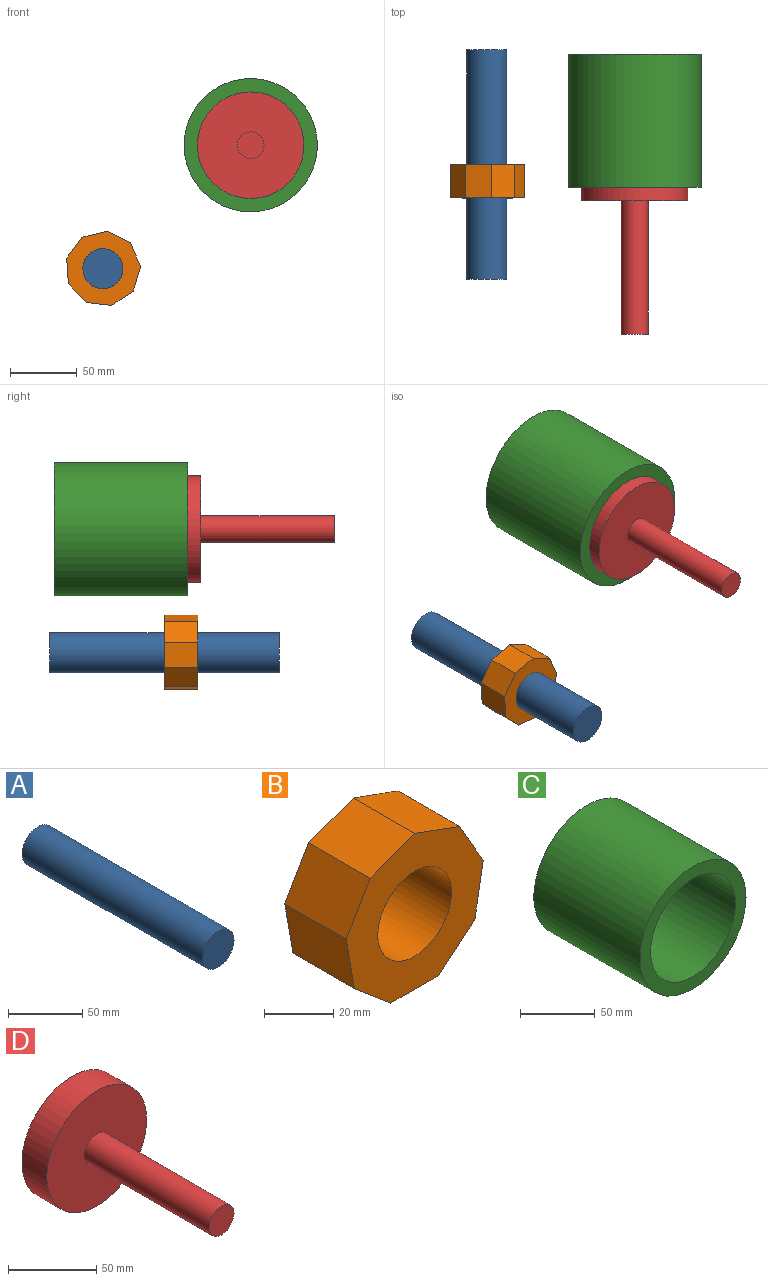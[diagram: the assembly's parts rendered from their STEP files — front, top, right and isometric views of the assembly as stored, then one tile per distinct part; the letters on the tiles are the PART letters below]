
ASSEMBLY  parts=4 mates=2
PART A: 3 faces, bbox 30x172.1x30 mm
  f0: cylinder r=15mm len=172.1mm, axis (0,1,0), area 16220mm2, adj f1,f2
  f1: plane 30x30mm, normal (0,-1,0), area 706.9mm2, adj f0
  f2: plane 30x30mm, normal (0,1,0), area 706.9mm2, adj f0
PART B: 12 faces, bbox 55.8x25x55 mm
  f0: plane 25x14.85mm, normal (0.64,0,-0.77), area 484.6mm2, adj f1,f8,f9,f10
  f1: plane 25x19.09mm, normal (0.98,0,-0.17), area 484.6mm2, adj f0,f2,f9,f10
  f2: plane 25x16.79mm, normal (0.87,0,0.5), area 484.6mm2, adj f1,f3,f9,f10
  f3: plane 25x18.21mm, normal (0.34,0,0.94), area 484.6mm2, adj f2,f4,f9,f10
  f4: plane 25x18.21mm, normal (-0.34,0,0.94), area 484.6mm2, adj f3,f5,f9,f10
  f5: plane 25x16.79mm, normal (-0.87,0,0.5), area 484.6mm2, adj f4,f6,f9,f10
  f6: plane 25x19.09mm, normal (-0.98,0,-0.17), area 484.6mm2, adj f5,f7,f9,f10
  f7: plane 25x14.85mm, normal (-0.64,0,-0.77), area 484.6mm2, adj f6,f8,f9,f10
  f8: plane 25x19.38mm, normal (0,0,-1), area 484.6mm2, adj f0,f7,f9,f10
  f9: plane 55.81x54.96mm, normal (0,-1,0), area 1615.7mm2, adj f0,f1,f2,f3,f4,f5,f6,f7
  f10: plane 55.81x54.96mm, normal (0,1,0), area 1615.7mm2, adj f0,f1,f2,f3,f4,f5,f6,f7
  f11: cylinder r=15mm len=30mm, axis (0,-1,0), area 2356.2mm2, adj f9,f10
PART C: 4 faces, bbox 100x100x100 mm
  f0: cylinder r=50mm len=100mm, axis (0,1,0), area 31415.9mm2, adj f1,f2
  f1: plane 100x100mm, normal (0,-1,0), area 2827.4mm2, adj f0,f3
  f2: plane 100x100mm, normal (0,1,0), area 2827.4mm2, adj f0,f3
  f3: cylinder r=40mm len=100mm, axis (0,-1,0), area 25132.7mm2, adj f1,f2
PART D: 5 faces, bbox 80x120x80 mm
  f0: cylinder r=40mm len=80mm, axis (0,1,0), area 5026.5mm2, adj f1,f2
  f1: plane 80x80mm, normal (0,-1,0), area 4712.4mm2, adj f0,f3
  f2: plane 80x80mm, normal (0,1,0), area 5026.5mm2, adj f0
  f3: cylinder r=10mm len=100mm, axis (0,1,0), area 6283.2mm2, adj f1,f4
  f4: plane 20x20mm, normal (0,-1,0), area 314.2mm2, adj f3
PLACE A t=(-149.35,20.82,-108.11)mm fixed
PLACE B rot(axis=(0,1,0),126.3deg) t=(-149.35,-65.23,-108.11)mm
PLACE C t=(-38.47,17.49,-15.46)mm fixed
PLACE D t=(-38.47,-72.51,-15.46)mm
MATE revolute B.f11 <-> A.f0  axis (0,-1,0) through (-149.35,-65.23,-108.11)mm
MATE slider C.f0 <-> D.f0  axis (0,-1,0) through (-38.47,-82.51,-15.46)mm
